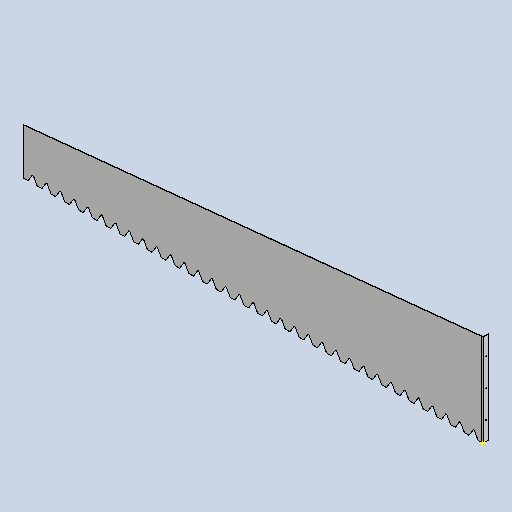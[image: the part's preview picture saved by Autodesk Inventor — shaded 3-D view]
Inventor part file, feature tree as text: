
AUTODESK INVENTOR PART (.ipt)
format: ipt  version: 2025 (Build 290162010, 162A)  size: 641,024 bytes
history: native  units: mm
features: other x5, sketch x3
ambient origin geometry x8: Origin, YZ Plane, XZ Plane, XY Plane, X Axis, Y Axis, Z Axis, Center Point
bodies: Solid1 (feature_tree)
feature tree (8):
  other  "MSC 071 ridge 1.ipt"
  sketch  "Sketch5"
  other  "A-Side Definition"
  other  "Solid1::MSC 071 ridge 1.ipt"
  other  "TaggingFeature1"
  sketch  "Sketch1"  dims[d0=10.0mm]
  sketch  "Sketch4"  dims[d1=2.0mm]
  other  "Definition1"
